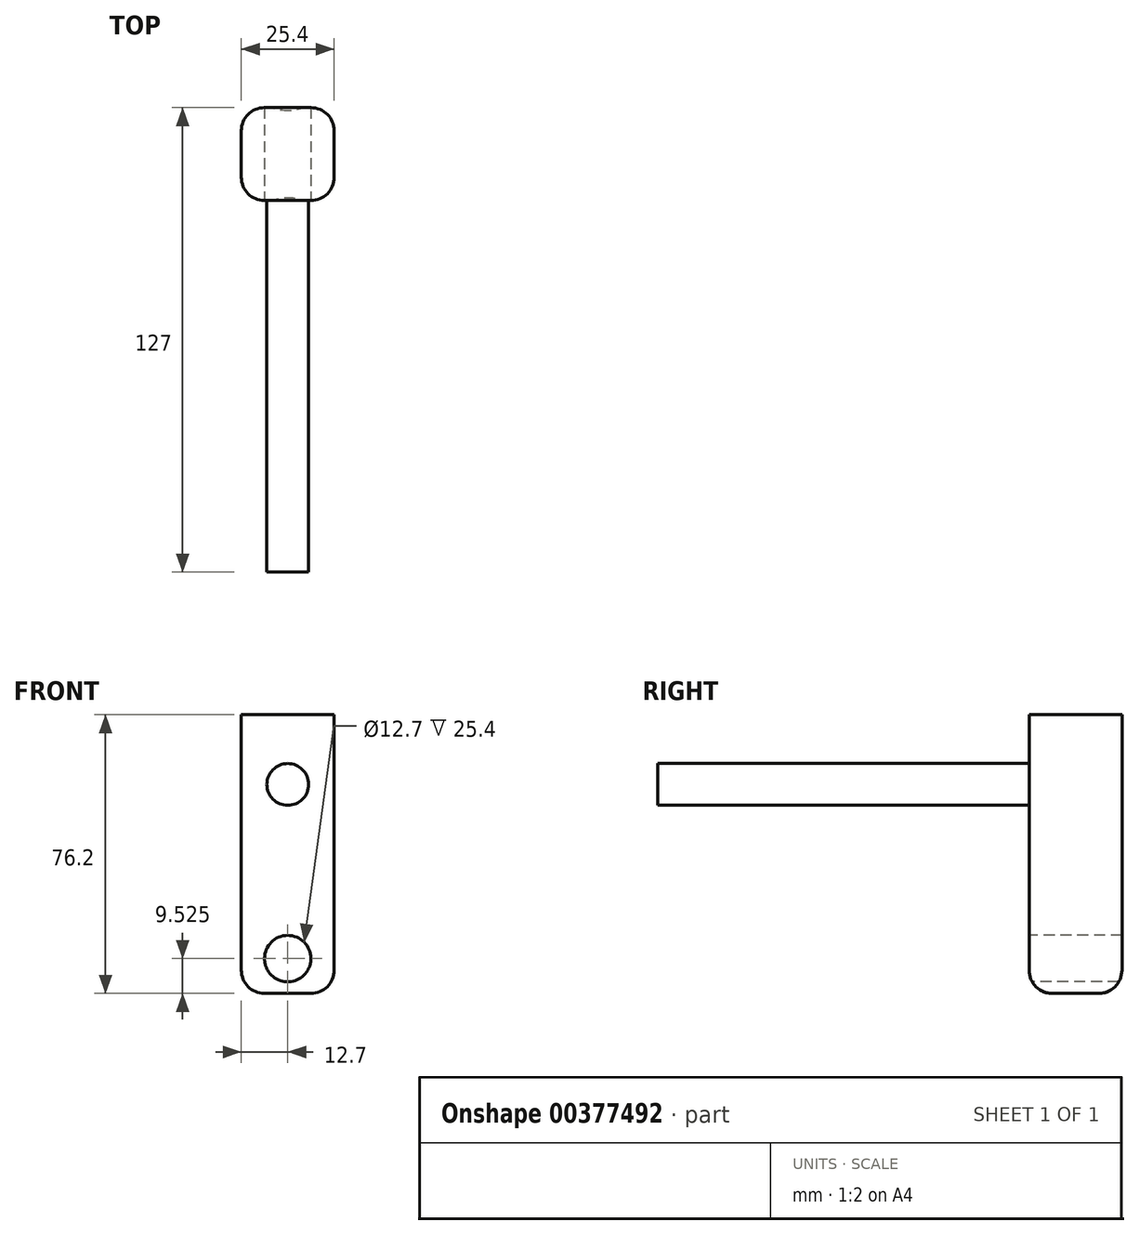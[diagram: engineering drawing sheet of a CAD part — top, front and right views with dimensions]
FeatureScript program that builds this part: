
annotation { "Feature Type Name" : "Feature", "Feature Type Description" : "" }
export const myFeature = defineFeature(function(context is Context, id is Id, definition is map)
    precondition{}
    {
        {
            var Q0;
            Q0=qCreatedBy(makeId("Front.planeOp"),FACE);
            var sketch = newSketch(context, id + "F0", { "sketchPlane" : qUnion([Q0])});
            skLineSegment(sketch, "E0", {"start": v(0, -76.2) * mm, "end": v(-12.7, -76.2) * mm});
            skLineSegment(sketch, "E1", {"start": v(-12.7, -76.2) * mm, "end": v(-12.7, 0) * mm});
            skLineSegment(sketch, "E2.MirrorCS", {"start": v(0, -76.2) * mm, "end": v(12.7, -76.2) * mm});
            skLineSegment(sketch, "E3.MirrorCS", {"start": v(12.7, -76.2) * mm, "end": v(12.7, 0) * mm});
            skLineSegment(sketch, "E4", {"start": v(-12.7, 0) * mm, "end": v(12.7, 0) * mm});
            skSolve(sketch);
        }
        {
            var Q0;
            Q0 = qSketchRegion(id + "F0", true);
            extrude(context, id + "F1", {"entities" : qUnion([Q0]), "depth" : 25.4 * mm});
        }
        {
            var Q0;
            Q0=makeQuery(id+"F1.opExtrude","CAP_FACE",FACE,{"disambiguationData":[OSD([sQuery(id+"F0.wireOp",EDGE,"E0"),sQuery(id+"F0.wireOp",EDGE,"E1"),sQuery(id+"F0.wireOp",EDGE,"E2.MirrorCS"),sQuery(id+"F0.wireOp",EDGE,"E3.MirrorCS"),sQuery(id+"F0.wireOp",EDGE,"E4")])],"isStart":false});
            var sketch = newSketch(context, id + "F2", { "sketchPlane" : qUnion([Q0])});
            skLineSegment(sketch, "E5", {"start": v(0, 0) * mm, "end": v(0, -76.2) * mm});
            skLineSegment(sketch, "E6", {"start": v(0, -76.2) * mm, "end": v(0, -38.1) * mm});
            skLineSegment(sketch, "E7", {"start": v(0, -38.1) * mm, "end": v(0, -57.15) * mm});
            skLineSegment(sketch, "E8", {"start": v(0, -57.15) * mm, "end": v(0, 0) * mm});
            skLineSegment(sketch, "E9", {"start": v(0, 0) * mm, "end": v(0, -38.1) * mm});
            skLineSegment(sketch, "E10", {"start": v(0, -19.05) * mm, "end": v(0, -38.1) * mm});
            skCircle(sketch, "E11", {"center": v(0, -19.05) * mm, "radius": 5.72 * mm});
            skLineSegment(sketch, "E12", {"start": v(0, -57.15) * mm, "end": v(0, -76.2) * mm});
            skLineSegment(sketch, "E13", {"start": v(0, -76.2) * mm, "end": v(0, -66.68) * mm});
            skSolve(sketch);
        }
        {
            var Q0;
            Q0 = qSketchRegion(id + "F2", true);
            extrude(context, id + "F3", {"entities" : qUnion([Q0]), "operationType" : NewBodyOperationType.ADD, "depth" : 101.6 * mm});
        }
        {
            var Q0;
            Q0=makeQuery(id+"F1.opExtrude","CAP_EDGE",EDGE,{"disambiguationData":[OSD([sQuery(id+"F0.wireOp",EDGE,"E3.MirrorCS")])],"isStart":false});
            var Q1;
            Q1=makeQuery(id+"F1.opExtrude","CAP_EDGE",EDGE,{"disambiguationData":[OSD([sQuery(id+"F0.wireOp",EDGE,"E3.MirrorCS")])],"isStart":true});
            var Q2;
            Q2=makeQuery(id+"F1.opExtrude","CAP_EDGE",EDGE,{"disambiguationData":[OSD([sQuery(id+"F0.wireOp",EDGE,"E1")])],"isStart":false});
            var Q3;
            Q3=makeQuery(id+"F1.opExtrude","CAP_EDGE",EDGE,{"disambiguationData":[OSD([sQuery(id+"F0.wireOp",EDGE,"E1")])],"isStart":true});
            fillet(context, id + "F4", {"entities" : qUnion([Q0, Q1, Q2, Q3]), "radius" : 6.35 * mm, "tangentPropagation" : true, "allowEdgeOverflow" : false});
        }
        {
            var Q0;
            Q0=makeQuery(id+"F1.opExtrude","CAP_FACE",FACE,{"disambiguationData":[OSD([sQuery(id+"F0.wireOp",EDGE,"E0"),sQuery(id+"F0.wireOp",EDGE,"E1"),sQuery(id+"F0.wireOp",EDGE,"E2.MirrorCS"),sQuery(id+"F0.wireOp",EDGE,"E3.MirrorCS"),sQuery(id+"F0.wireOp",EDGE,"E4")])],"isStart":false});
            var sketch = newSketch(context, id + "F5", { "sketchPlane" : qUnion([Q0])});
            skLineSegment(sketch, "E14", {"start": v(0, 0) * mm, "end": v(0, -76.2) * mm});
            skLineSegment(sketch, "E15", {"start": v(0, 0) * mm, "end": v(0, -38.1) * mm});
            skLineSegment(sketch, "E16", {"start": v(0, -38.1) * mm, "end": v(0, -76.2) * mm});
            skLineSegment(sketch, "E17", {"start": v(0, -76.2) * mm, "end": v(0, -57.15) * mm});
            skLineSegment(sketch, "E18", {"start": v(0, -57.15) * mm, "end": v(0, -66.68) * mm});
            skSolve(sketch);
        }
        {
            var Q0;
            Q0=sQuery(id+"F5.wireOp",VERTEX,"E18.end");
            var Q1;
            Q1=makeQuery(id+"F1.opExtrude","SWEPT_BODY",BODY,{"disambiguationData":[OSD([sQuery(id+"F0.wireOp",EDGE,"E0"),sQuery(id+"F0.wireOp",EDGE,"E1"),sQuery(id+"F0.wireOp",EDGE,"E2.MirrorCS"),sQuery(id+"F0.wireOp",EDGE,"E3.MirrorCS"),sQuery(id+"F0.wireOp",EDGE,"E4")])]});
            hole(context, id + "F6", {"style" : HoleStyle.SIMPLE, "endStyle" : HoleEndStyle.BLIND, "holeDiameter" : 12.7 * mm, "holeDepth" : 254 * mm, "tappedDepth" : 12.7 * mm, "tapClearance" : 3, "locations" : qUnion([Q0]), "scope" : qUnion([Q1])});
        }
        {
            var Q0;
            Q0=makeQuery(id+"F1.opExtrude","SWEPT_EDGE",EDGE,{"disambiguationData":[OSD([sQuery(id+"F0.wireOp",EDGE,"E2.MirrorCS"),sQuery(id+"F0.wireOp",EDGE,"E3.MirrorCS")])]});
            var Q1;
            Q1=makeQuery(id+"F1.opExtrude","SWEPT_EDGE",EDGE,{"disambiguationData":[OSD([sQuery(id+"F0.wireOp",EDGE,"E0"),sQuery(id+"F0.wireOp",EDGE,"E1")])]});
            fillet(context, id + "F7", {"entities" : qUnion([Q0, Q1]), "radius" : 6.35 * mm, "tangentPropagation" : true, "allowEdgeOverflow" : false});
        }
    });
